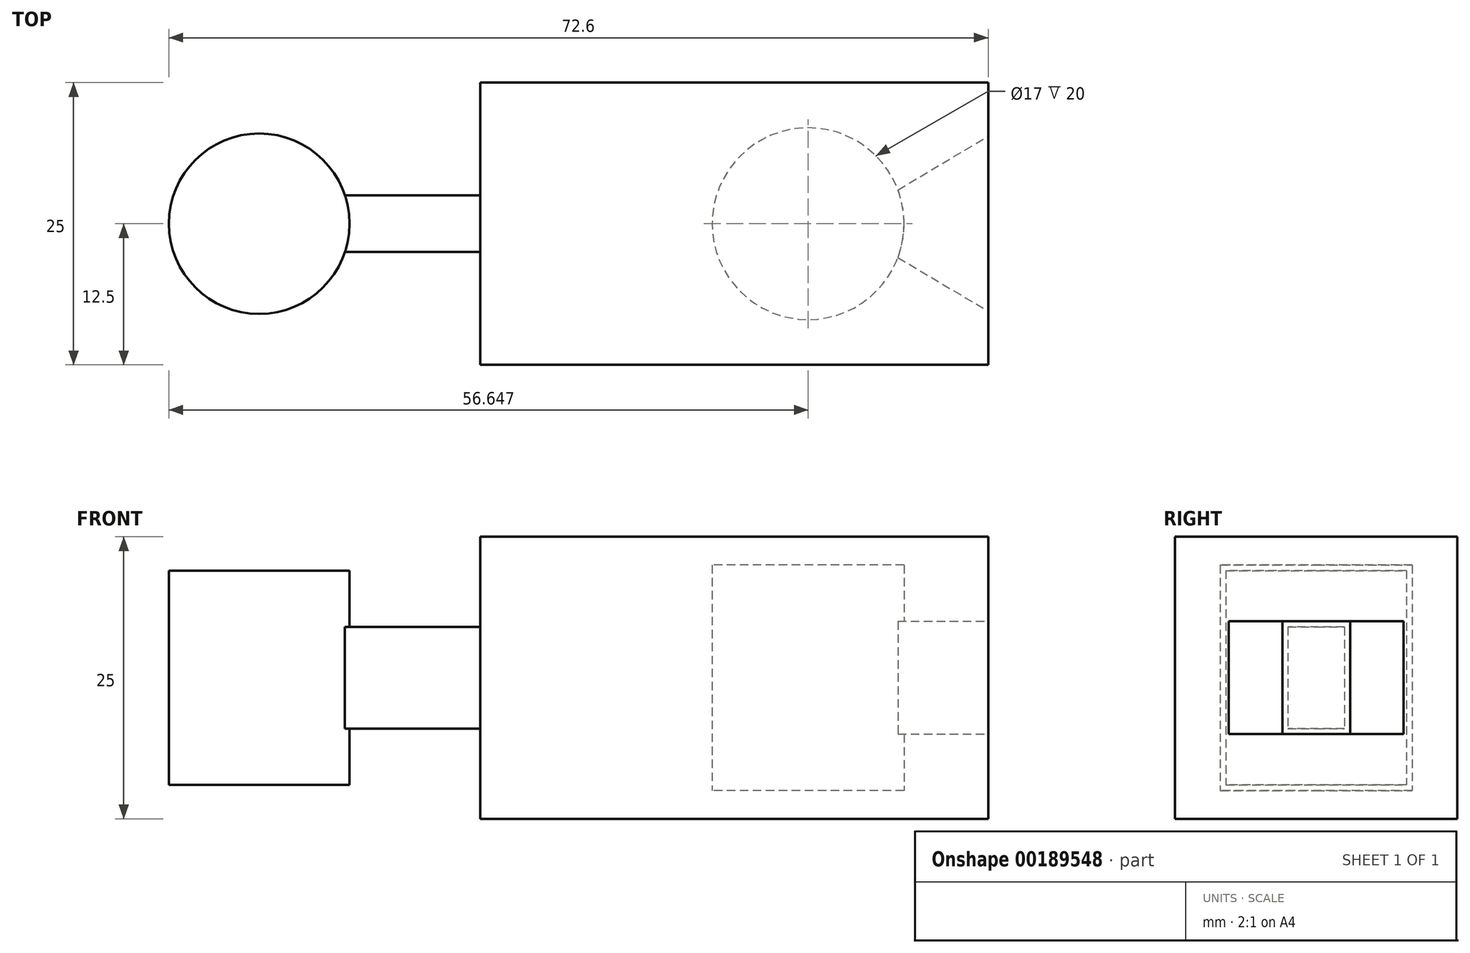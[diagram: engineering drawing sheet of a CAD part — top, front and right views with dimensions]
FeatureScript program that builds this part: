
annotation { "Feature Type Name" : "Feature", "Feature Type Description" : "" }
export const myFeature = defineFeature(function(context is Context, id is Id, definition is map)
    precondition{}
    {
        {
            var Q0;
            Q0=qCreatedBy(makeId("Top.planeOp"),FACE);
            var sketch = newSketch(context, id + "F0", { "sketchPlane" : qUnion([Q0])});
            skLineSegment(sketch, "E0.bottom", {"start": v(-22.5, 12.5) * mm, "end": v(22.5, 12.5) * mm});
            skLineSegment(sketch, "E0.top", {"start": v(-22.5, -12.5) * mm, "end": v(22.5, -12.5) * mm});
            skLineSegment(sketch, "E0.left", {"start": v(-22.5, 12.5) * mm, "end": v(-22.5, -12.5) * mm});
            skLineSegment(sketch, "E0.right", {"start": v(22.5, 12.5) * mm, "end": v(22.5, 3) * mm});
            skPoint(sketch, "E0.middle", {"position": v(0, 0) * mm});
            skLineSegment(sketch, "E1.bottom", {"start": v(-22.5, 2.5) * mm, "end": v(-34.5, 2.5) * mm});
            skLineSegment(sketch, "E1.top", {"start": v(-22.5, -2.5) * mm, "end": v(-34.5, -2.5) * mm});
            skLineSegment(sketch, "E1.left", {"start": v(-22.5, 2.5) * mm, "end": v(-22.5, -2.5) * mm});
            skPoint(sketch, "E1.middle", {"position": v(-28.5, 0) * mm});
            skPoint(sketch, "E1.middle.positionSnap0", {"position": v(-22.5, 0) * mm});
            skPoint(sketch, "E1.centerSnap0", {"position": v(-22.5, 0) * mm});
            skPoint(sketch, "E2.startSnap0", {"position": v(-28.5, -2.5) * mm});
            skLineSegment(sketch, "E3.bottom", {"start": v(22.5, 3) * mm, "end": v(14.5, 3) * mm});
            skLineSegment(sketch, "E3.top", {"start": v(22.5, -3) * mm, "end": v(14.5, -3) * mm});
            skPoint(sketch, "E3.middle", {"position": v(18.5, 0) * mm});
            skLineSegment(sketch, "E4.trimOffspring", {"start": v(22.5, -3) * mm, "end": v(22.5, -12.5) * mm});
            skPoint(sketch, "E5.orphan", {"position": v(22.5, 0) * mm});
            skLineSegment(sketch, "E6.right", {"start": v(22.5, 12.5) * mm, "end": v(22.5, -12.5) * mm});
            skLineSegment(sketch, "E7.right", {"start": v(22.5, 0) * mm, "end": v(22.5, 0) * mm});
            skCircle(sketch, "E8", {"center": v(-42.1, 0) * mm, "radius": 8 * mm});
            skCircle(sketch, "E9", {"center": v(6.55, 0) * mm, "radius": 8.5 * mm});
            skLineSegment(sketch, "E10", {"start": v(14.5, 3) * mm, "end": v(22.5, 7.75) * mm});
            skLineSegment(sketch, "E11", {"start": v(14.5, -3) * mm, "end": v(22.5, -7.75) * mm});
            skSolve(sketch);
        }
        {
            var Q0;
            {var subQ4=sQuery(id+"F0.wireOp",EDGE,"E0.bottom");Q0=makeQuery(id+"F0.imprint","IMPRINT",FACE,{"disambiguationData":[TD([[makeQuery(id+"F0.imprint","IMPRINT",EDGE,{"derivedFrom":subQ4}),-1.0]])]});}
            var Q1;
            {var subQ0=sQuery(id+"F0.wireOp",EDGE,"E9");var subQ1=makeQuery(id+"F0.imprint","INTERSECT",VERTEX,{"derivedFrom":[sQuery(id+"F0.wireOp",EDGE,"E3.bottom"),subQ0,sQuery(id+"F0.wireOp",EDGE,"E10")]});Q1=makeQuery(id+"F0.imprint","IMPRINT",FACE,{"disambiguationData":[TD([[makeQuery(id+"F0.imprint","IMPRINT",EDGE,{"disambiguationData":[TD([[subQ1,-1.0]])],"derivedFrom":subQ0}),1.0]])]});}
            var Q2;
            {var subQ0=sQuery(id+"F0.wireOp",EDGE,"E3.top");Q2=makeQuery(id+"F0.imprint","IMPRINT",FACE,{"disambiguationData":[TD([[makeQuery(id+"F0.imprint","IMPRINT",EDGE,{"derivedFrom":subQ0}),1.0]])]});}
            var Q3;
            {var subQ0=sQuery(id+"F0.wireOp",EDGE,"E3.bottom");Q3=makeQuery(id+"F0.imprint","IMPRINT",FACE,{"disambiguationData":[TD([[makeQuery(id+"F0.imprint","IMPRINT",EDGE,{"derivedFrom":subQ0}),1.0]])]});}
            var Q4;
            {var subQ0=sQuery(id+"F0.wireOp",EDGE,"E3.bottom");Q4=makeQuery(id+"F0.imprint","IMPRINT",FACE,{"disambiguationData":[TD([[makeQuery(id+"F0.imprint","IMPRINT",EDGE,{"derivedFrom":subQ0}),-1.0]])]});}
            extrude(context, id + "F1", {"entities" : qUnion([Q0, Q1, Q2, Q3, Q4]), "endBound" : BoundingType.SYMMETRIC, "depth" : 25 * mm});
        }
        {
            var Q0;
            {var subQ0=sQuery(id+"F0.wireOp",EDGE,"E9");var subQ1=makeQuery(id+"F0.imprint","INTERSECT",VERTEX,{"derivedFrom":[sQuery(id+"F0.wireOp",EDGE,"E3.bottom"),subQ0]});Q0=makeQuery(id+"F0.imprint","IMPRINT",FACE,{"disambiguationData":[TD([[makeQuery(id+"F0.imprint","IMPRINT",EDGE,{"disambiguationData":[TD([[subQ1,-1.0]])],"derivedFrom":subQ0}),1.0]])]});}
            var Q1;
            Q1=sQuery(id+"F0.wireOp",EDGE,"E9");
            extrude(context, id + "F2", {"entities" : qUnion([Q0]), "operationType" : NewBodyOperationType.REMOVE, "surfaceEntities" : qUnion([Q1]), "endBound" : BoundingType.SYMMETRIC, "depth" : 20 * mm});
        }
        {
            var Q0;
            {var subQ0=sQuery(id+"F0.wireOp",EDGE,"E1.bottom");Q0=makeQuery(id+"F0.imprint","IMPRINT",FACE,{"disambiguationData":[TD([[makeQuery(id+"F0.imprint","IMPRINT",EDGE,{"derivedFrom":subQ0}),1.0]])]});}
            extrude(context, id + "F3", {"entities" : qUnion([Q0]), "operationType" : NewBodyOperationType.ADD, "endBound" : BoundingType.SYMMETRIC, "depth" : 9 * mm});
        }
        {
            var Q0;
            {var subQ0=sQuery(id+"F0.wireOp",EDGE,"E8");var subQ1=makeQuery(id+"F0.imprint","INTERSECT",VERTEX,{"derivedFrom":[sQuery(id+"F0.wireOp",EDGE,"E1.bottom"),subQ0]});Q0=makeQuery(id+"F0.imprint","IMPRINT",FACE,{"disambiguationData":[TD([[makeQuery(id+"F0.imprint","IMPRINT",EDGE,{"disambiguationData":[TD([[subQ1,-1.0]])],"derivedFrom":subQ0}),1.0]])]});}
            extrude(context, id + "F4", {"entities" : qUnion([Q0]), "operationType" : NewBodyOperationType.ADD, "endBound" : BoundingType.SYMMETRIC, "depth" : 19 * mm});
        }
        {
            var Q0;
            {var subQ0=sQuery(id+"F0.wireOp",EDGE,"E3.bottom");Q0=makeQuery(id+"F0.imprint","IMPRINT",FACE,{"disambiguationData":[TD([[makeQuery(id+"F0.imprint","IMPRINT",EDGE,{"derivedFrom":subQ0}),-1.0]])]});}
            var Q1;
            {var subQ0=sQuery(id+"F0.wireOp",EDGE,"E3.bottom");Q1=makeQuery(id+"F0.imprint","IMPRINT",FACE,{"disambiguationData":[TD([[makeQuery(id+"F0.imprint","IMPRINT",EDGE,{"derivedFrom":subQ0}),1.0]])]});}
            var Q2;
            {var subQ0=sQuery(id+"F0.wireOp",EDGE,"E3.top");Q2=makeQuery(id+"F0.imprint","IMPRINT",FACE,{"disambiguationData":[TD([[makeQuery(id+"F0.imprint","IMPRINT",EDGE,{"derivedFrom":subQ0}),1.0]])]});}
            extrude(context, id + "F5", {"entities" : qUnion([Q0, Q1, Q2]), "operationType" : NewBodyOperationType.REMOVE, "endBound" : BoundingType.SYMMETRIC, "depth" : 10 * mm});
        }
    });
